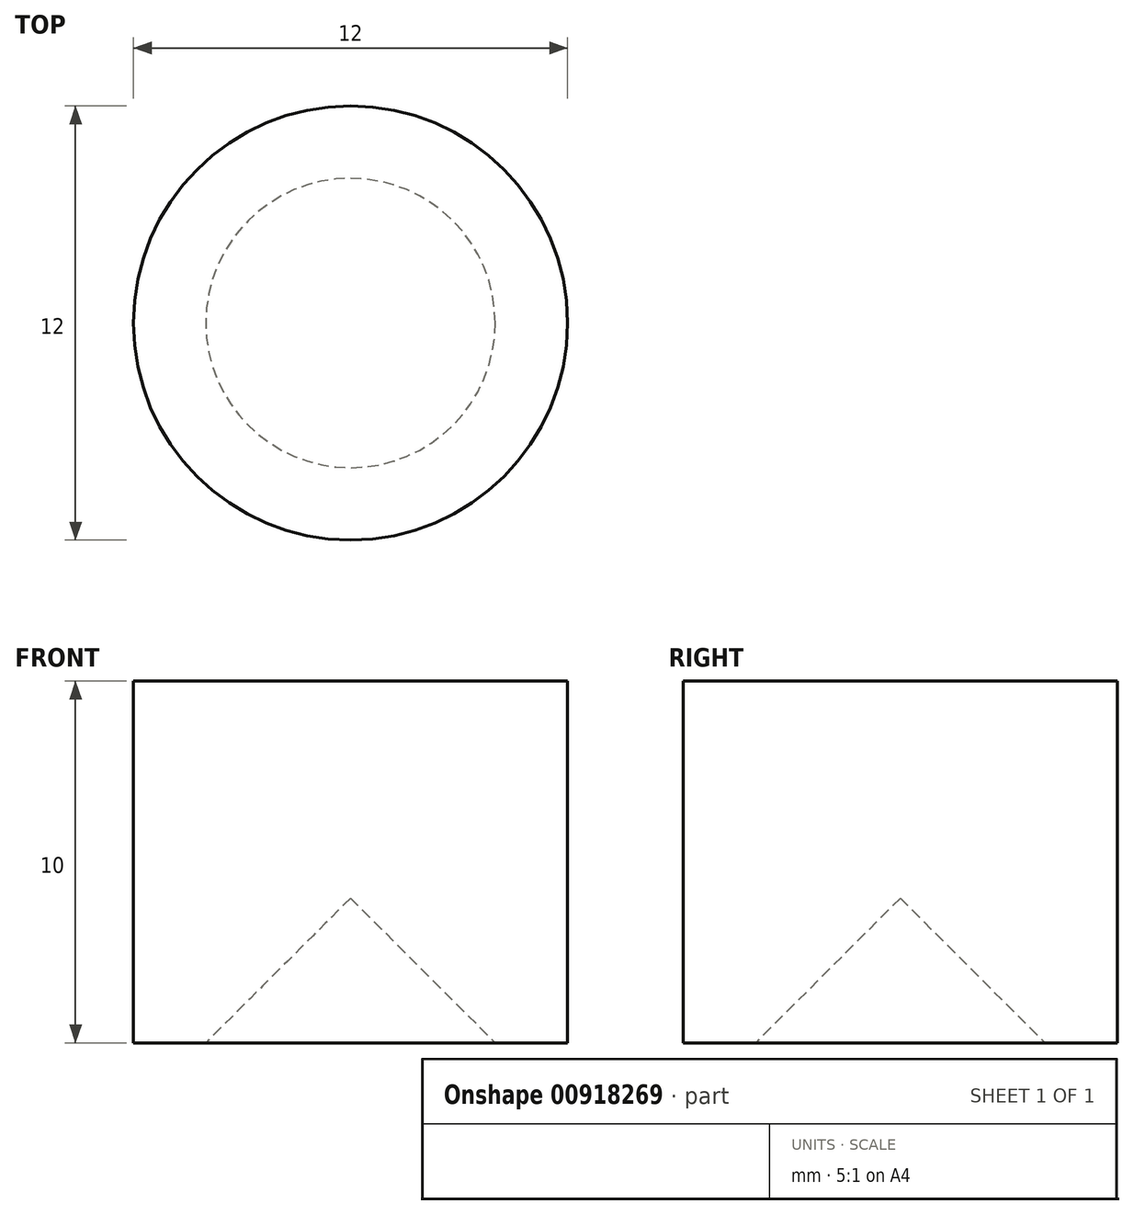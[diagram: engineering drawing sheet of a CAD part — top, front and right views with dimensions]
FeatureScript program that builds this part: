
annotation { "Feature Type Name" : "Feature", "Feature Type Description" : "" }
export const myFeature = defineFeature(function(context is Context, id is Id, definition is map)
    precondition{}
    {
        {
            var Q0;
            Q0=qCreatedBy(makeId("Front.planeOp"),FACE);
            var sketch = newSketch(context, id + "F0", { "sketchPlane" : qUnion([Q0])});
            skLineSegment(sketch, "E0", {"start": v(0, 0) * mm, "end": v(0, 19.12) * mm, "construction": true});
            skLineSegment(sketch, "E1", {"start": v(-6, 0) * mm, "end": v(-6, 10) * mm});
            skLineSegment(sketch, "E2", {"start": v(-6, 10) * mm, "end": v(0, 10) * mm});
            skLineSegment(sketch, "E3", {"start": v(-6, 0) * mm, "end": v(-4, 0) * mm});
            skLineSegment(sketch, "E4", {"start": v(-4, 0) * mm, "end": v(0, 4) * mm});
            skLineSegment(sketch, "E5", {"start": v(0, 4) * mm, "end": v(0, 10) * mm});
            skSolve(sketch);
        }
        {
            var Q0;
            Q0=qSketchRegion(id+"F0",true);
            var Q1;
            Q1=sQuery(id+"F0.wireOp",EDGE,"E0");
            revolve(context, id + "F1", {"surfaceOperationType" : NewSurfaceOperationType.NEW, "entities" : qUnion([Q0]), "axis" : qUnion([Q1]), "revolveType" : RevolveType.FULL});
        }
    });
